# Revit family: Door_Screen-Sliding-Phantom_Screens-Single_Parting-Retractable_Door_Screens-TW2
name_source: partatom
category: Specialty Equipment
revit_build: Autodesk Revit 2017 (Build: 20160225_1515(x64)
units: mm (PartAtom-declared; Revit-internal decimal feet)

## family parameters
Always vertical = Yes
Cut with Voids When Loaded = No
OmniClass Number = 23.30.60.21
OmniClass Title = Insect Screens
Part Type = Normal
Room Calculation Point = No
Round Connector Dimension = Use Diameter
Shared = No
Work Plane-Based = No

## types (2) — shared parameters
Assembly Code = B2010300
Finish = Metal-Aluminum-Phantom_Screens-Classic_White
Finish Screen = Fabric-Privacy_Mesh-Phantom_Screens-Mermet_E-Screen_7505-Charcoal
Manufacturer = Phantom Mfg. (Int'l) Ltd.
Product Documentation Link = https://www.phantomscreens.com
Product Name = Retractable Door Screens
Product Page URL = https://www.phantomscreens.com
Thickness = 0' - 1 23/32"
Type Comments = Single Parting Door
URL = https://www.phantomscreens.com

## per-type parameters (varying)
| type | Description | Magnetic Latch | Model |
| Magnetic Handle | Phantom retractable door screen with magnet catch | Yes | Magnet Latching System |
| Latch Handle | Phantom retractable door screen with latching handle | No | Latch and Release System |

type visibility flags (boolean, named after types; folded from table):
- Magnetic Handle: Yes: (none)
- Latch Handle: Yes: Latch Handle

## geometry (parser evidence)
native form markers: Extrusion x10, Sweep x17
no freeform markers — native parametric forms only
